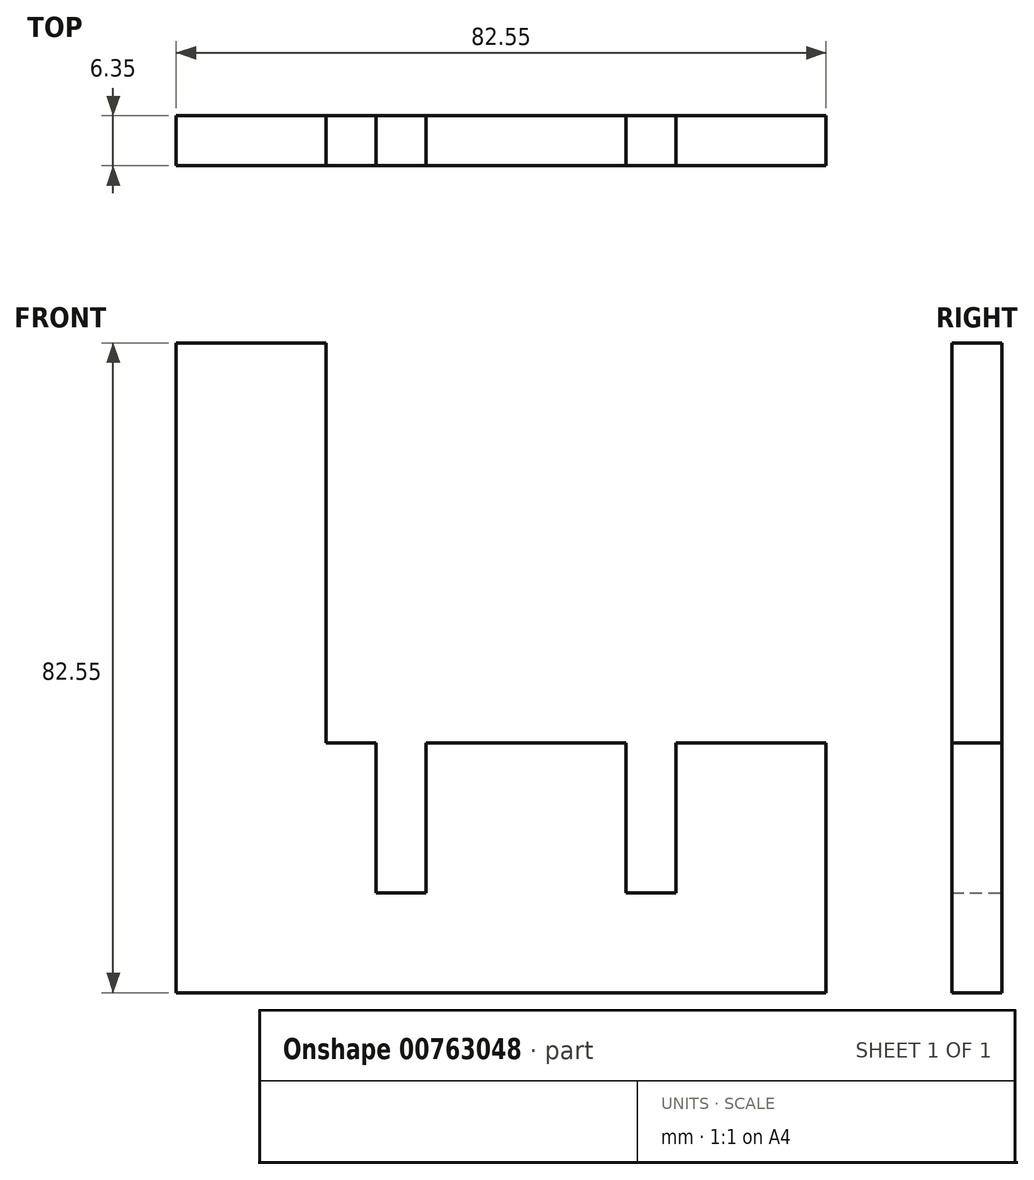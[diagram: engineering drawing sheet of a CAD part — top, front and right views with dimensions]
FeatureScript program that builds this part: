
annotation { "Feature Type Name" : "Feature", "Feature Type Description" : "" }
export const myFeature = defineFeature(function(context is Context, id is Id, definition is map)
    precondition{}
    {
        {
            var Q0;
            Q0=qCreatedBy(makeId("Front.planeOp"),FACE);
            var sketch = newSketch(context, id + "F0", { "sketchPlane" : qUnion([Q0])});
            skLineSegment(sketch, "E0.bottom", {"start": v(0, 0) * mm, "end": v(82.55, 0) * mm});
            skLineSegment(sketch, "E0.top", {"start": v(0, 82.55) * mm, "end": v(19.05, 82.55) * mm});
            skLineSegment(sketch, "E0.left", {"start": v(0, 0) * mm, "end": v(0, 82.55) * mm});
            skLineSegment(sketch, "E0.right", {"start": v(82.55, 0) * mm, "end": v(82.55, 31.75) * mm});
            skLineSegment(sketch, "E1.top", {"start": v(82.55, 31.75) * mm, "end": v(63.5, 31.75) * mm});
            skLineSegment(sketch, "E1.right", {"start": v(19.05, 82.55) * mm, "end": v(19.05, 31.75) * mm});
            skLineSegment(sketch, "E2.top", {"start": v(25.4, 12.7) * mm, "end": v(31.75, 12.7) * mm});
            skLineSegment(sketch, "E2.left", {"start": v(25.4, 31.75) * mm, "end": v(25.4, 12.7) * mm});
            skLineSegment(sketch, "E2.right", {"start": v(31.75, 31.75) * mm, "end": v(31.75, 12.7) * mm});
            skLineSegment(sketch, "E3.top", {"start": v(57.15, 12.7) * mm, "end": v(63.5, 12.7) * mm});
            skLineSegment(sketch, "E3.left", {"start": v(57.15, 31.75) * mm, "end": v(57.15, 12.7) * mm});
            skLineSegment(sketch, "E3.right", {"start": v(63.5, 31.75) * mm, "end": v(63.5, 12.7) * mm});
            skLineSegment(sketch, "E4.trimOffspring", {"start": v(25.4, 31.75) * mm, "end": v(19.05, 31.75) * mm});
            skLineSegment(sketch, "E5.trimOffspring", {"start": v(57.15, 31.75) * mm, "end": v(31.75, 31.75) * mm});
            skSolve(sketch);
        }
        {
            var Q0;
            Q0 = qSketchRegion(id + "F0", true);
            extrude(context, id + "F1", {"entities" : qUnion([Q0]), "depth" : 6.35 * mm, "offsetDistance" : 25.4 * mm});
        }
    });
